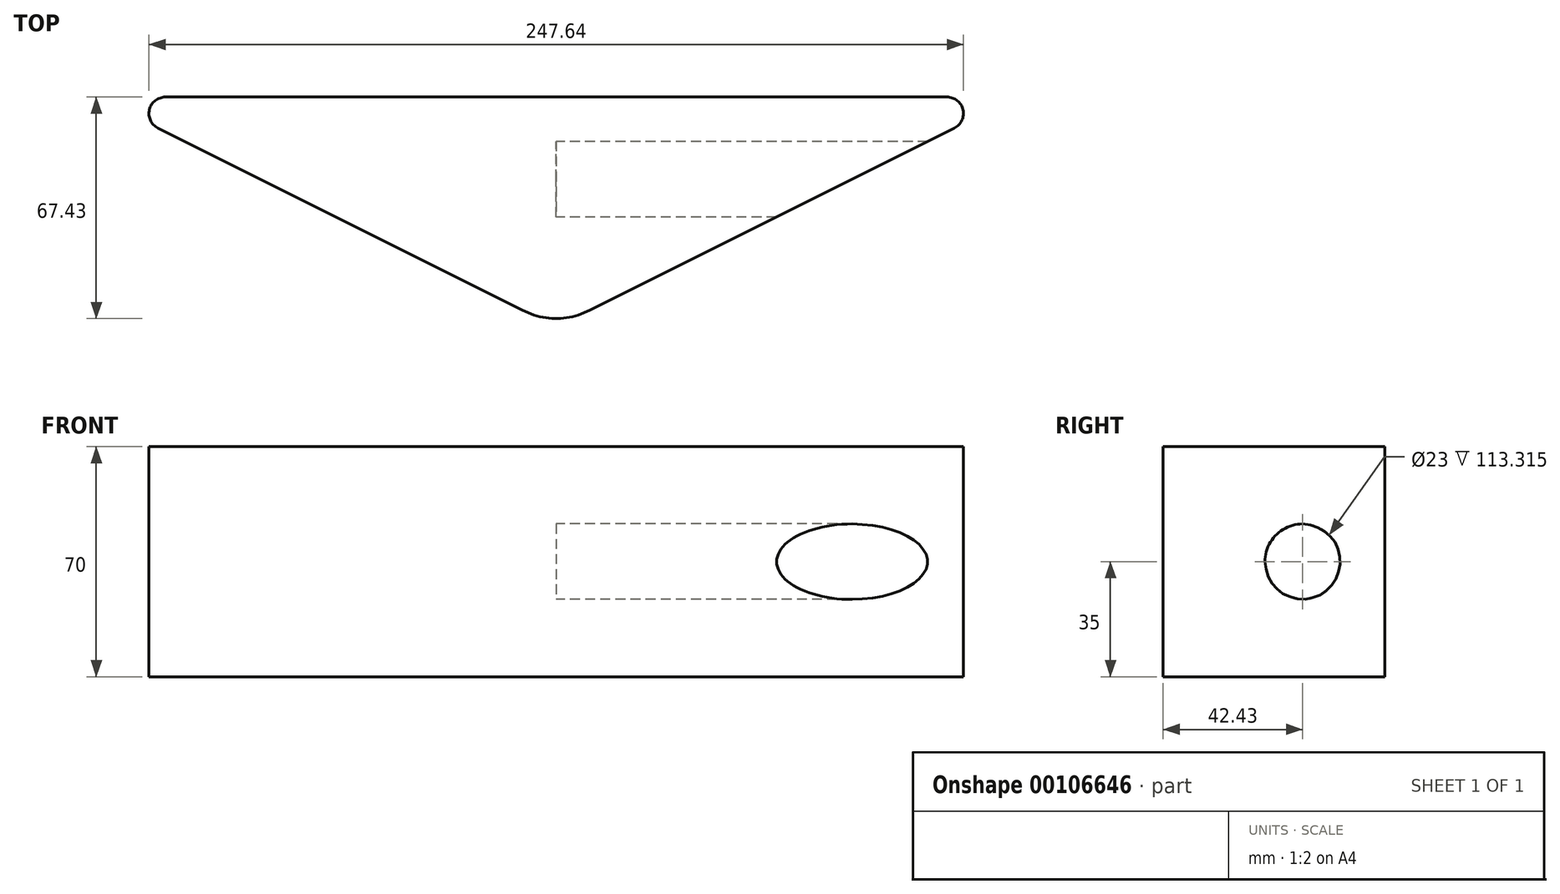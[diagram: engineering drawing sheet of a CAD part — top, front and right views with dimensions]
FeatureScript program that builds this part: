
annotation { "Feature Type Name" : "Feature", "Feature Type Description" : "" }
export const myFeature = defineFeature(function(context is Context, id is Id, definition is map)
    precondition{}
    {
        {
            var Q0;
            Q0=qCreatedBy(makeId("Top.planeOp"),FACE);
            var sketch = newSketch(context, id + "F0", { "sketchPlane" : qUnion([Q0])});
            skLineSegment(sketch, "E0", {"start": v(-140, 70) * mm, "end": v(140, 70) * mm});
            skLineSegment(sketch, "E1", {"start": v(140, 70) * mm, "end": v(0, 0) * mm});
            skLineSegment(sketch, "E2", {"start": v(0, 0) * mm, "end": v(-140, 70) * mm});
            skSolve(sketch);
        }
        {
            var Q0;
            Q0=makeQuery(id+"F0.imprint","IMPRINT",FACE,{"disambiguationData":[TD([[makeQuery(id+"F0.imprint","IMPRINT",EDGE,{"derivedFrom":sQuery(id+"F0.wireOp",EDGE,"E0")}),-1.0]])]});
            extrude(context, id + "F1", {"entities" : qUnion([Q0]), "depth" : 70 * mm});
        }
        {
            var Q0;
            Q0=makeQuery(id+"F1.opExtrude","SWEPT_EDGE",EDGE,{"disambiguationData":[OSD([sQuery(id+"F0.wireOp",EDGE,"E0"),sQuery(id+"F0.wireOp",EDGE,"E1")])]});
            var Q1;
            Q1=makeQuery(id+"F1.opExtrude","SWEPT_EDGE",EDGE,{"disambiguationData":[OSD([sQuery(id+"F0.wireOp",EDGE,"E0"),sQuery(id+"F0.wireOp",EDGE,"E2")])]});
            fillet(context, id + "F2", {"entities" : qUnion([Q0, Q1]), "radius" : 5 * mm, "tangentPropagation" : true, "allowEdgeOverflow" : false});
        }
        {
            var Q0;
            Q0=makeQuery(id+"F1.opExtrude","SWEPT_EDGE",EDGE,{"disambiguationData":[OSD([sQuery(id+"F0.wireOp",EDGE,"E1"),sQuery(id+"F0.wireOp",EDGE,"E2")])]});
            fillet(context, id + "F3", {"entities" : qUnion([Q0]), "radius" : 23 * mm, "tangentPropagation" : true, "rho" : 0.5, "crossSection" : FilletCrossSection.CONIC, "allowEdgeOverflow" : false});
        }
        {
            var Q0;
            Q0=qCreatedBy(makeId("Right.planeOp"),FACE);
            var sketch = newSketch(context, id + "F4", { "sketchPlane" : qUnion([Q0])});
            skLineSegment(sketch, "E3.bottom", {"start": v(0, 0) * mm, "end": v(70, 0) * mm});
            skLineSegment(sketch, "E3.top", {"start": v(0, 70) * mm, "end": v(70, 70) * mm});
            skLineSegment(sketch, "E3.left", {"start": v(0, 0) * mm, "end": v(0, 70) * mm});
            skLineSegment(sketch, "E3.right", {"start": v(70, 0) * mm, "end": v(70, 70) * mm});
            skPoint(sketch, "E4", {"position": v(45, 35) * mm});
            skPoint(sketch, "E4.positionSnap0", {"position": v(45, 70) * mm});
            skPoint(sketch, "E4.positionSnap1", {"position": v(70, 35) * mm});
            skSolve(sketch);
        }
        {
            var Q0;
            Q0=sQuery(id+"F4.wireOp",VERTEX,"E4");
            var Q1;
            Q1=makeQuery(id+"F1.opExtrude","SWEPT_BODY",BODY,{"disambiguationData":[OSD([sQuery(id+"F0.wireOp",EDGE,"E0"),sQuery(id+"F0.wireOp",EDGE,"E1"),sQuery(id+"F0.wireOp",EDGE,"E2")])]});
            hole(context, id + "F5", {"style" : HoleStyle.SIMPLE, "endStyle" : HoleEndStyle.THROUGH, "oppositeDirection" : true, "holeDiameter" : 23 * mm, "locations" : qUnion([Q0]), "scope" : qUnion([Q1]), "isTappedThrough" : true});
        }
    });
